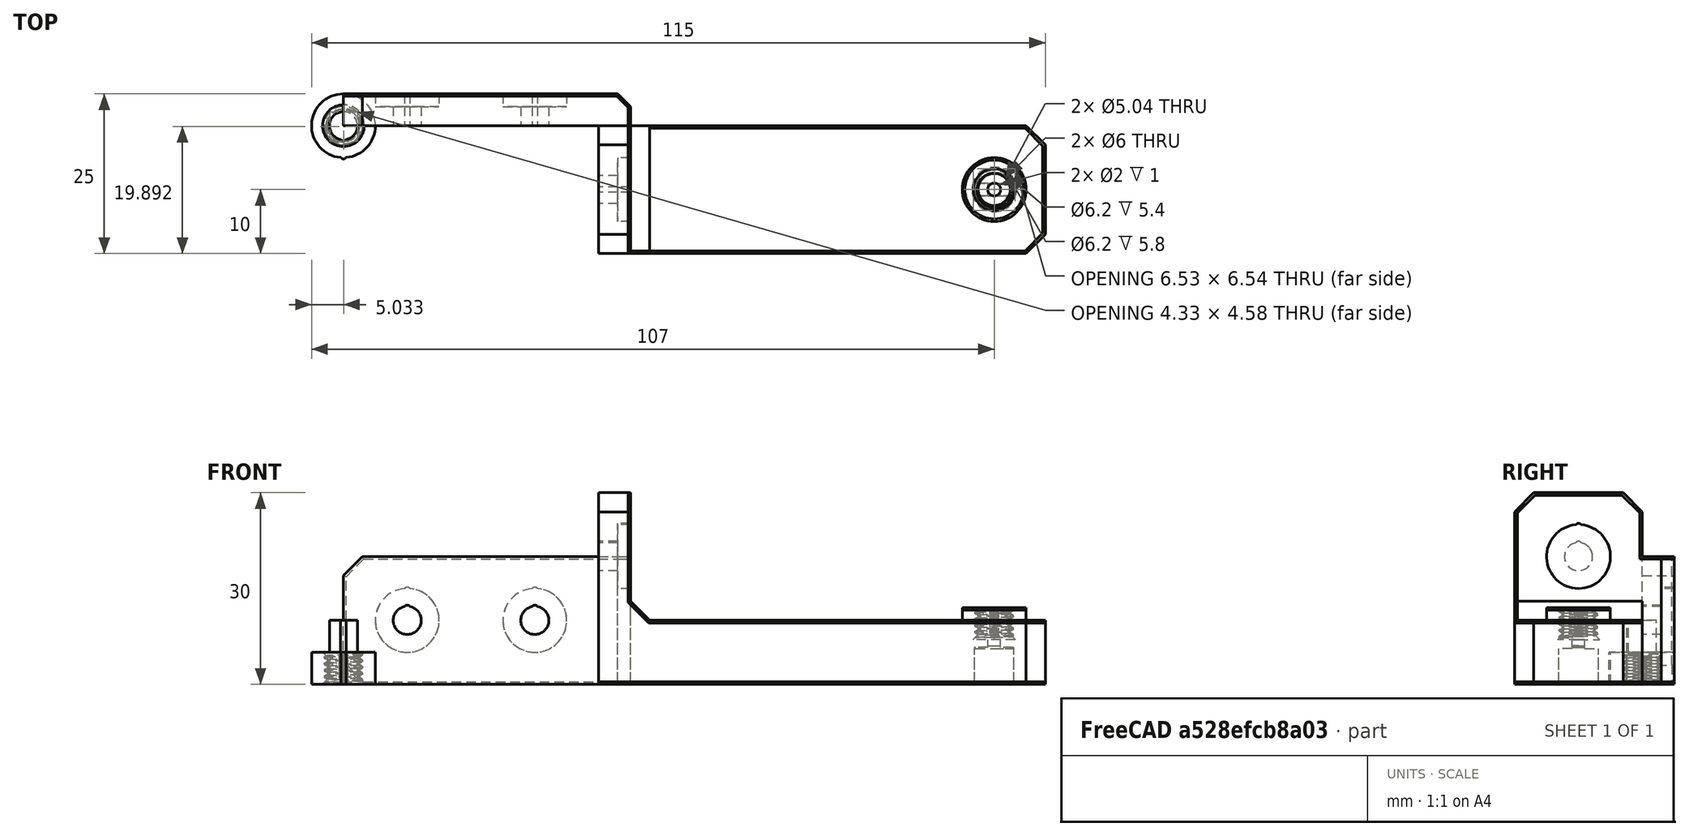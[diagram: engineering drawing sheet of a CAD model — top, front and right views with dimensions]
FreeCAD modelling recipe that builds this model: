
FCSTD DOCUMENT  (FreeCAD 0.18R16146 (Git))
Label: loli-bear-rev-direct-guide
License: All rights reserved
LicenseURL: http://en.wikipedia.org/wiki/All_rights_reserved
objects: Part::Cylinder×8, Part::Box×7, Part::Feature×6, Part::MultiFuse×6, Part::Chamfer×6, Part::Cut×4
note: 37 computed .brp shape members not serialized (recipe doc carries the construction recipe); baked Part::Feature solids carry a one-line shape summary decoded from their .brp

FEATURE [Part::Box] Box  label="Cube"
  AttacherType = Attacher::AttachEngine3D
  Height = 20
  Length = 45
  Width = 5
FEATURE [Part::Box] Box001  label="Cube001"
  AttacherType = Attacher::AttachEngine3D
  Height = 30
  Length = 5
  Placement = pos=(40,-20,0) rot=(0,0,1;0rad)
  Width = 20
FEATURE [Part::Box] Box002  label="Cube002"
  AttacherType = Attacher::AttachEngine3D
  Height = 10
  Length = 70
  Placement = pos=(40,-20,0) rot=(0,0,1;0rad)
  Width = 20
FEATURE [Part::Feature] Part__Feature  label="00100106009"
  shape: bbox 11.42 x 11.42 x 5.051 mm, 37 faces (baked)
FEATURE [Part::Cylinder] Cylinder
  Angle = 360
  AttacherType = Attacher::AttachEngine3D
  Height = 5
  Radius = 4.5
FEATURE [Part::Cut] Cut  label="m6-thread"
  Base = -> Cylinder
  Tool = -> Part__Feature
FEATURE [Part::Feature] Cut001  label="m6-thread001"
  Placement = pos=(102,-10,7) rot=(0,0,1;0rad)
  shape: bbox 6.692 x 6.692 x 5.039 mm, 11 faces (baked)
FEATURE [Part::Cylinder] Cylinder002
  Angle = 360
  AttacherType = Attacher::AttachEngine3D
  Height = 2
  Placement = pos=(102,-10,10) rot=(0,0,1;0rad)
  Radius = 5
FEATURE [Part::Cylinder] Cylinder003  label="filament-path"
  Angle = 360
  AttacherType = Attacher::AttachEngine3D
  Height = 12
  Placement = pos=(102,-10,0) rot=(0,0,1;0rad)
  Radius = 1
FEATURE [Part::Cylinder] Cylinder004  label="Cylinder003"
  Angle = 360
  AttacherType = Attacher::AttachEngine3D
  Height = 6
  Radius = 3.1
FEATURE [Part::Box] Box003  label="Cube003"
  AttacherType = Attacher::AttachEngine3D
  Height = 0.2
  Length = 10
  Placement = pos=(1,-5,5.8) rot=(0,0,1;0rad)
  Width = 10
FEATURE [Part::Box] Box004  label="Cube004"
  AttacherType = Attacher::AttachEngine3D
  Height = 0.2
  Length = 10
  Placement = pos=(-11,-5,5.8) rot=(0,0,1;0rad)
  Width = 10
FEATURE [Part::Box] Box005  label="Cube005"
  AttacherType = Attacher::AttachEngine3D
  Height = 0.4
  Length = 10
  Placement = pos=(-5,1,5.6) rot=(0,0,1;0rad)
  Width = 10
FEATURE [Part::Box] Box006  label="Cube006"
  AttacherType = Attacher::AttachEngine3D
  Height = 0.4
  Length = 10
  Placement = pos=(-5,-11,5.6) rot=(0,0,1;0rad)
  Width = 10
FEATURE [Part::MultiFuse] Fusion003
  Shapes = -> [Box003,Box004,Box005,Box006]
FEATURE [Part::Cut] Cut005
  Base = -> Cylinder004
  Placement = pos=(102,-10,0) rot=(0,0,1;0rad)
  Tool = -> Fusion003
FEATURE [Part::Chamfer] Chamfer
  Base = -> Box001
  Edges = 2 edges r=3: [Edge10,Edge12]
FEATURE [Part::Chamfer] Chamfer002
  Base = -> Box002
  Edges = 2 edges r=3: [Edge5,Edge7]
FEATURE [Part::MultiFuse] Fusion
  Shapes = -> [Chamfer,Chamfer002]
FEATURE [Part::Chamfer] Chamfer003
  Base = -> Fusion
  Edges = 1 edges r=3: [Edge39]
FEATURE [Part::MultiFuse] Fusion006
  Shapes = -> [Cut005,Cylinder003,Cut001]
FEATURE [Part::Chamfer] Chamfer004
  Base = -> Box
  Edges = 2 edges r=3: [Edge2,Edge4]
FEATURE [Part::Chamfer] Chamfer005
  Base = -> Chamfer004
  Edges = 1 edges r=2: [Edge15]
FEATURE [Part::MultiFuse] Fusion007
  Shapes = -> [Cylinder002,Chamfer003,Chamfer005]
FEATURE [Part::Cut] Cut006
  Base = -> Fusion007
  Tool = -> Fusion006
FEATURE [Part::Feature] Cut006001  label="Cut007"
  shape: bbox 110 x 25 x 30 mm, 47 faces (baked)
FEATURE [Part::Chamfer] Chamfer006
  Base = -> Cut006001
  Edges = 27 edges r=0.4: [Edge1,Edge3,Edge4,Edge5,Edge6,Edge8,Edge13,Edge14,Edge17,Edge18,Edge91,Edge94,Edge101,Edge102,Edge104,Edge106,Edge111,Edge114,Edge116,Edge117,Edge121,Edge123,Edge125,Edge126,Edge127,Edge129,Edge130]
FEATURE [Part::Cylinder] Cylinder005  label="Cylinder004"
  Angle = 360
  AttacherType = Attacher::AttachEngine3D
  Height = 5
  Placement = pos=(0,-4.7,0) rot=(0,0,1;0rad)
  Radius = 0.5
FEATURE [Part::Cylinder] Cylinder006  label="Cylinder005"
  Angle = 360
  AttacherType = Attacher::AttachEngine3D
  Height = 10
  Placement = pos=(0,-1.9,0) rot=(0,0,1;0rad)
  Radius = 0.5
FEATURE [Part::Cylinder] Cylinder007  label="Cylinder006"
  Angle = 360
  AttacherType = Attacher::AttachEngine3D
  Height = 5
  Radius = 5
FEATURE [Part::Cylinder] Cylinder008  label="Cylinder007"
  Angle = 360
  AttacherType = Attacher::AttachEngine3D
  Height = 10
  Radius = 2.2
FEATURE [Part::MultiFuse] Fusion008  label="m4"
  Shapes = -> [Cylinder005,Cylinder007,Cylinder008,Cylinder006]
FEATURE [Part::Feature] Fusion008001  label="m005"
  Placement = pos=(10,8,10) rot=(0,0.707107,-0.707107;3.14159rad)
  shape: bbox 10 x 10 x 10.2 mm, 7 faces (baked)
FEATURE [Part::Feature] Fusion008003  label="m007"
  Placement = pos=(48,-10,20) rot=(0.57735,0.57735,-0.57735;4.18879rad)
  shape: bbox 10 x 10 x 10.2 mm, 7 faces (baked)
FEATURE [Part::Feature] Fusion008004  label="m008"
  Placement = pos=(30,8,10) rot=(0,0.707107,-0.707107;3.14159rad)
  shape: bbox 10 x 10 x 10.2 mm, 7 faces (baked)
FEATURE [Part::MultiFuse] Fusion008005
  Shapes = -> [Fusion008001,Fusion008004,Fusion008003]
FEATURE [Part::Cut] Cut006002
  Base = -> Chamfer006
  Tool = -> Fusion008005
